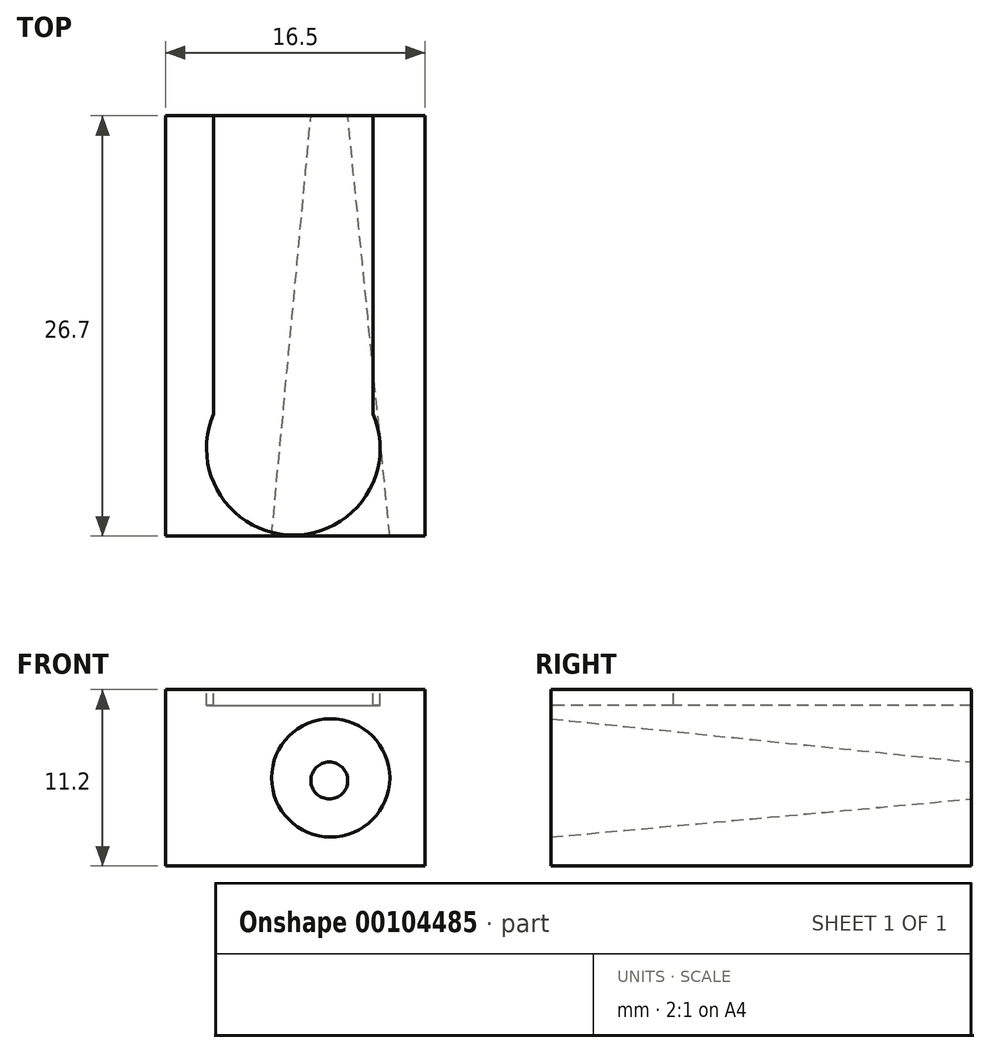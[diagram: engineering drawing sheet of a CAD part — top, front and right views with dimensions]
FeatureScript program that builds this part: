
annotation { "Feature Type Name" : "Feature", "Feature Type Description" : "" }
export const myFeature = defineFeature(function(context is Context, id is Id, definition is map)
    precondition{}
    {
        {
            var Q0;
            Q0=qCreatedBy(makeId("Front.planeOp"),FACE);
            var sketch = newSketch(context, id + "F0", { "sketchPlane" : qUnion([Q0])});
            skLineSegment(sketch, "E0.bottom", {"start": v(-7.75, 4.76) * mm, "end": v(8.75, 4.76) * mm});
            skLineSegment(sketch, "E0.top", {"start": v(-7.75, -6.44) * mm, "end": v(8.75, -6.44) * mm});
            skLineSegment(sketch, "E0.left", {"start": v(-7.75, 4.76) * mm, "end": v(-7.75, -6.44) * mm});
            skLineSegment(sketch, "E0.right", {"start": v(8.75, 4.76) * mm, "end": v(8.75, -6.44) * mm});
            skSolve(sketch);
        }
        {
            var Q0;
            Q0 = qSketchRegion(id + "F0", true);
            extrude(context, id + "F1", {"entities" : qUnion([Q0]), "depth" : 26.7 * mm});
        }
        {
            var Q0;
            Q0=makeQuery(id+"F1.opExtrude","SWEPT_FACE",FACE,{"disambiguationData":[OSD([sQuery(id+"F0.wireOp",EDGE,"E0.bottom")])]});
            var sketch = newSketch(context, id + "F2", { "sketchPlane" : qUnion([Q0])});
            skPoint(sketch, "E1.end.orphan", {"position": v(-43.57, 0) * mm});
            skPoint(sketch, "E1.start.orphan", {"position": v(0, 7.67) * mm});
            skLineSegment(sketch, "E2", {"start": v(-4.69, 0) * mm, "end": v(-4.69, -18.94) * mm});
            skLineSegment(sketch, "E3", {"start": v(5.44, 0) * mm, "end": v(5.44, -18.94) * mm});
            skArc(sketch, "E4", {"start": v(-4.69, -18.94) * mm, "mid": v(0.37, -26.64) * mm, "end": v(5.44, -18.94) * mm});
            skLineSegment(sketch, "E5", {"start": v(-4.69, 0) * mm, "end": v(5.44, 0) * mm});
            skSolve(sketch);
        }
        {
            var Q0;
            Q0 = qSketchRegion(id + "F2", true);
            extrude(context, id + "F3", {"entities" : qUnion([Q0]), "operationType" : NewBodyOperationType.REMOVE, "oppositeDirection" : true, "depth" : 1 * mm});
        }
        {
            var Q0;
            Q0=makeQuery(id+"F1.opExtrude","CAP_FACE",FACE,{"disambiguationData":[OSD([sQuery(id+"F0.wireOp",EDGE,"E0.bottom"),sQuery(id+"F0.wireOp",EDGE,"E0.top"),sQuery(id+"F0.wireOp",EDGE,"E0.left"),sQuery(id+"F0.wireOp",EDGE,"E0.right")])],"isStart":false});
            var sketch = newSketch(context, id + "F4", { "sketchPlane" : qUnion([Q0])});
            skCircle(sketch, "E6", {"center": v(2.75, -0.85) * mm, "radius": 3.75 * mm});
            skSolve(sketch);
        }
        {
            var Q0;
            Q0=qCreatedBy(makeId("Front.planeOp"),FACE);
            var sketch = newSketch(context, id + "F5", { "sketchPlane" : qUnion([Q0])});
            skCircle(sketch, "E7", {"center": v(2.66, -1.02) * mm, "radius": 1.17 * mm});
            skSolve(sketch);
        }
        {
            var Q1;
            Q1 = qSketchRegion(id + "F5", true);
            var Q2;
            Q2 = qSketchRegion(id + "F4", true);
            loft(context, id + "F6", {"operationType" : NewBodyOperationType.REMOVE, "sheetProfilesArray" : [{ "sheetProfileEntities" : qUnion([Q1]) }, { "sheetProfileEntities" : qUnion([Q2]) }]});
        }
    });
